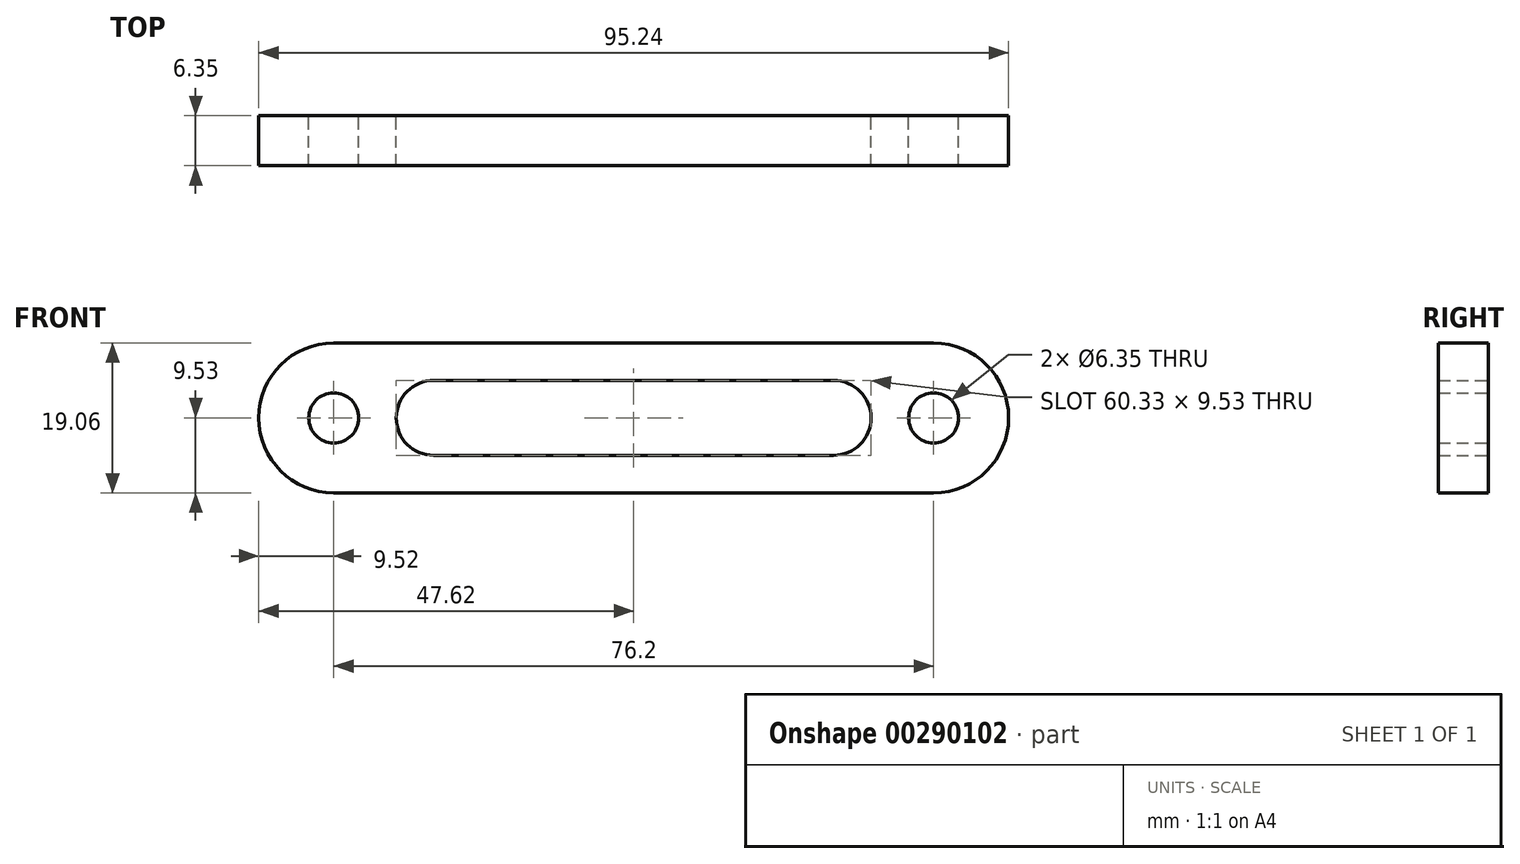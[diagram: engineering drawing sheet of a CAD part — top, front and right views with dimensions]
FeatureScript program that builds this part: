
annotation { "Feature Type Name" : "Feature", "Feature Type Description" : "" }
export const myFeature = defineFeature(function(context is Context, id is Id, definition is map)
    precondition{}
    {
        {
            var Q0;
            Q0=qCreatedBy(makeId("Front.planeOp"),FACE);
            var sketch = newSketch(context, id + "F0", { "sketchPlane" : qUnion([Q0])});
            skLineSegment(sketch, "E0.bottom", {"start": v(25.4, 4.76) * mm, "end": v(-25.4, 4.76) * mm});
            skLineSegment(sketch, "E0.top", {"start": v(25.4, -4.76) * mm, "end": v(-25.4, -4.76) * mm});
            skPoint(sketch, "E0.middle", {"position": v(0, 0) * mm});
            skLineSegment(sketch, "E1.bottom", {"start": v(38.1, 9.53) * mm, "end": v(-38.1, 9.52) * mm});
            skLineSegment(sketch, "E1.top", {"start": v(38.1, -9.52) * mm, "end": v(-38.1, -9.53) * mm});
            skArc(sketch, "E2", {"start": v(-25.4, 4.76) * mm, "mid": v(-30.16, 0) * mm, "end": v(-25.4, -4.76) * mm});
            skArc(sketch, "E3", {"start": v(25.4, -4.76) * mm, "mid": v(30.16, 0) * mm, "end": v(25.4, 4.76) * mm});
            skArc(sketch, "E4", {"start": v(-38.1, 9.52) * mm, "mid": v(-47.62, 0) * mm, "end": v(-38.1, -9.53) * mm});
            skArc(sketch, "E5", {"start": v(38.1, -9.52) * mm, "mid": v(47.62, 0) * mm, "end": v(38.1, 9.53) * mm});
            skCircle(sketch, "E6", {"center": v(38.1, 0) * mm, "radius": 3.18 * mm});
            skCircle(sketch, "E7", {"center": v(-38.1, 0) * mm, "radius": 3.18 * mm});
            skSolve(sketch);
        }
        {
            var Q0;
            Q0=makeQuery(id+"F0.imprint","IMPRINT",FACE,{"disambiguationData":[TD([[makeQuery(id+"F0.imprint","IMPRINT",EDGE,{"derivedFrom":sQuery(id+"F0.wireOp",EDGE,"E0.bottom")}),-1.0]])]});
            extrude(context, id + "F1", {"entities" : qUnion([Q0]), "depth" : 6.35 * mm});
        }
    });
